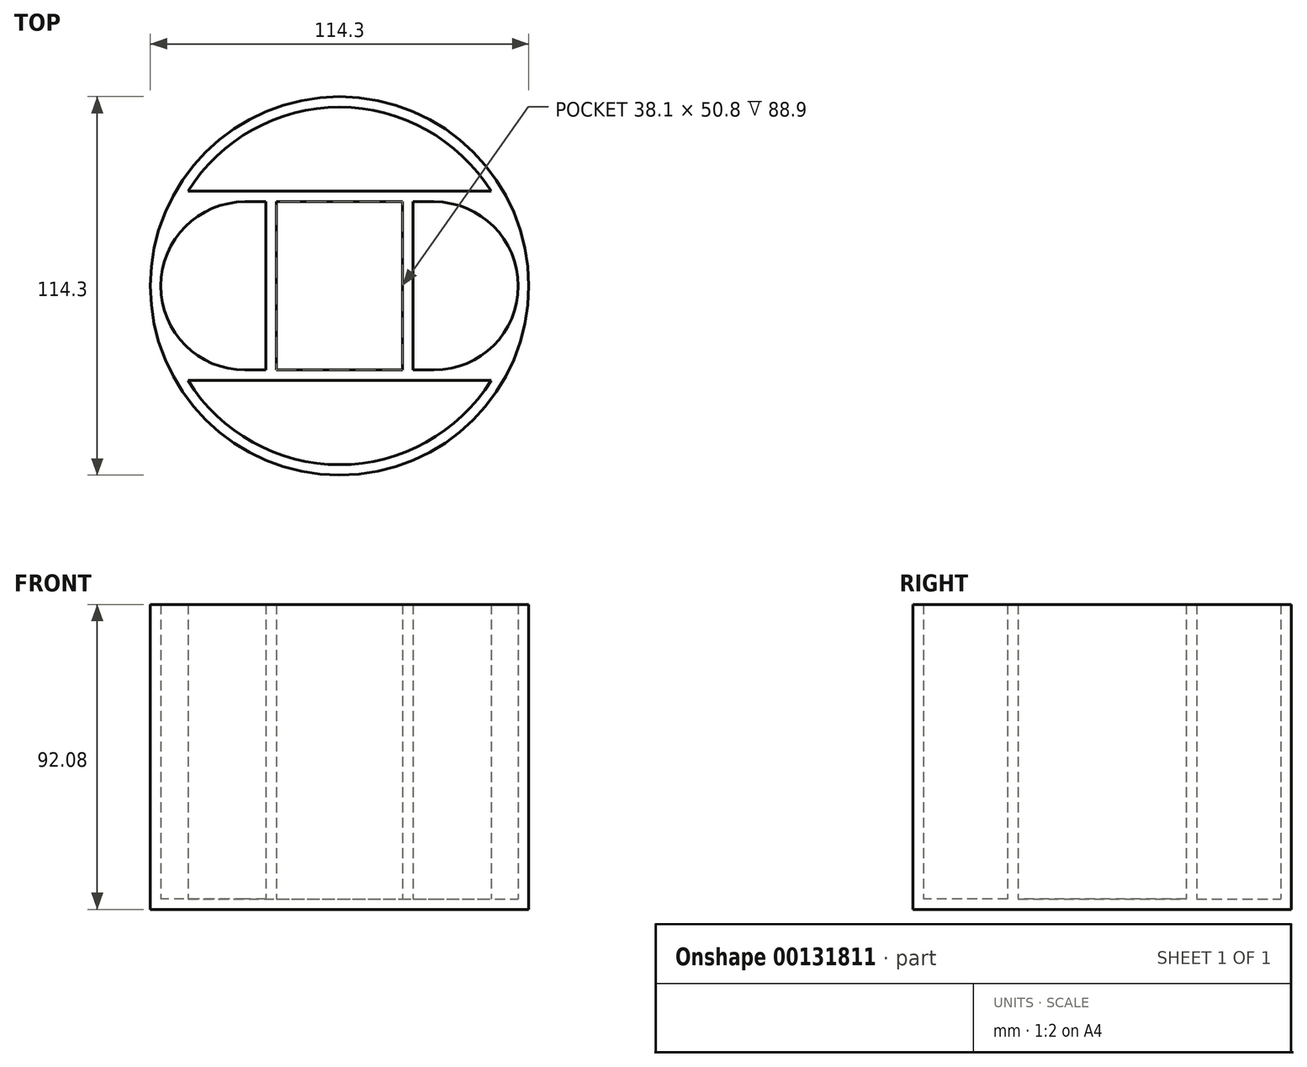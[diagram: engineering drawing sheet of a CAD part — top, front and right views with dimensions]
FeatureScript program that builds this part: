
annotation { "Feature Type Name" : "Feature", "Feature Type Description" : "" }
export const myFeature = defineFeature(function(context is Context, id is Id, definition is map)
    precondition{}
    {
        {
            var Q0;
            Q0=qCreatedBy(makeId("Top.planeOp"),FACE);
            var sketch = newSketch(context, id + "F2", { "sketchPlane" : qUnion([Q0])});
            skLineSegment(sketch, "E0.bottom", {"start": v(-22.23, 0) * mm, "end": v(-28.58, 0) * mm});
            skLineSegment(sketch, "E0.top", {"start": v(-22.22, 50.8) * mm, "end": v(-28.58, 50.8) * mm});
            skLineSegment(sketch, "E0.right", {"start": v(-28.58, 0) * mm, "end": v(-28.58, 50.8) * mm, "construction": true});
            skArc(sketch, "E1", {"start": v(-28.58, 50.8) * mm, "mid": v(-53.98, 25.4) * mm, "end": v(-28.58, 0) * mm});
            skLineSegment(sketch, "E2", {"start": v(-22.23, 0) * mm, "end": v(-22.23, 50.8) * mm});
            skLineSegment(sketch, "E3", {"start": v(0, 0) * mm, "end": v(0, 50.8) * mm, "construction": true});
            skLineSegment(sketch, "E4", {"start": v(0, 0) * mm, "end": v(-19.05, 0) * mm});
            skLineSegment(sketch, "E5", {"start": v(-19.05, 0) * mm, "end": v(-19.05, 50.8) * mm});
            skLineSegment(sketch, "E6", {"start": v(-19.05, 50.8) * mm, "end": v(0, 50.8) * mm});
            skCircle(sketch, "E7", {"center": v(0, 25.4) * mm, "radius": 57.15 * mm});
            skLineSegment(sketch, "E8.MirrorCS", {"start": v(19.05, 50.8) * mm, "end": v(0, 50.8) * mm});
            skLineSegment(sketch, "E9.MirrorCS", {"start": v(19.05, 0) * mm, "end": v(19.05, 50.8) * mm});
            skLineSegment(sketch, "E10.MirrorCS", {"start": v(0, 0) * mm, "end": v(19.05, 0) * mm});
            skLineSegment(sketch, "E11.MirrorCS", {"start": v(22.23, 0) * mm, "end": v(28.58, 0) * mm});
            skLineSegment(sketch, "E12.MirrorCS", {"start": v(22.23, 0) * mm, "end": v(22.23, 50.8) * mm});
            skLineSegment(sketch, "E13.MirrorCS", {"start": v(22.22, 50.8) * mm, "end": v(28.58, 50.8) * mm});
            skArc(sketch, "E14.MirrorCS", {"start": v(28.58, 50.8) * mm, "mid": v(53.98, 25.4) * mm, "end": v(28.58, 0) * mm});
            skArc(sketch, "E15.0", {"start": v(-45.8, -3.18) * mm, "mid": v(0, -28.58) * mm, "end": v(45.8, -3.17) * mm});
            skLineSegment(sketch, "E16", {"start": v(-45.8, 53.98) * mm, "end": v(45.8, 53.98) * mm});
            skLineSegment(sketch, "E17", {"start": v(0, 50.8) * mm, "end": v(0, 53.98) * mm, "construction": true});
            skLineSegment(sketch, "E18", {"start": v(-45.8, -3.18) * mm, "end": v(45.8, -3.18) * mm});
            skLineSegment(sketch, "E19", {"start": v(0, 0) * mm, "end": v(0, -3.18) * mm, "construction": true});
            skLineSegment(sketch, "E20", {"start": v(-19.05, 0) * mm, "end": v(-22.23, 0) * mm, "construction": true});
            skArc(sketch, "E21.trimOffspring", {"start": v(45.8, 53.98) * mm, "mid": v(0, 79.38) * mm, "end": v(-45.8, 53.98) * mm});
            skSolve(sketch);
        }
        {
            var Q0;
            Q0=makeQuery(id+"F2.imprint","IMPRINT",FACE,{"disambiguationData":[TD([[makeQuery(id+"F2.imprint","IMPRINT",EDGE,{"derivedFrom":sQuery(id+"F2.wireOp",EDGE,"E0.bottom")}),1.0]])]});
            var Q1;
            Q1=makeQuery(id+"F2.imprint","IMPRINT",FACE,{"disambiguationData":[TD([[makeQuery(id+"F2.imprint","IMPRINT",EDGE,{"derivedFrom":sQuery(id+"F2.wireOp",EDGE,"E0.left")}),-1.0]])]});
            extrude(context, id + "F3", {"entities" : qUnion([Q0, Q1]), "depth" : 88.9 * mm});
        }
        {
            var Q0;
            Q0=makeQuery(id+"F3.opExtrude","CAP_FACE",FACE,{"disambiguationData":[OSD([sQuery(id+"F2.wireOp",EDGE,"E0.bottom"),sQuery(id+"F2.wireOp",EDGE,"E0.top"),sQuery(id+"F2.wireOp",EDGE,"E1"),sQuery(id+"F2.wireOp",EDGE,"E2"),sQuery(id+"F2.wireOp",EDGE,"E4"),sQuery(id+"F2.wireOp",EDGE,"E5"),sQuery(id+"F2.wireOp",EDGE,"E6"),sQuery(id+"F2.wireOp",EDGE,"E7"),sQuery(id+"F2.wireOp",EDGE,"E8.MirrorCS"),sQuery(id+"F2.wireOp",EDGE,"E9.MirrorCS"),sQuery(id+"F2.wireOp",EDGE,"E10.MirrorCS"),sQuery(id+"F2.wireOp",EDGE,"E11.MirrorCS"),sQuery(id+"F2.wireOp",EDGE,"E12.MirrorCS"),sQuery(id+"F2.wireOp",EDGE,"E13.MirrorCS"),sQuery(id+"F2.wireOp",EDGE,"E14.MirrorCS"),sQuery(id+"F2.wireOp",EDGE,"E15.0"),sQuery(id+"F2.wireOp",EDGE,"E16"),sQuery(id+"F2.wireOp",EDGE,"E18"),sQuery(id+"F2.wireOp",EDGE,"E21.trimOffspring")])],"isStart":true});
            var sketch = newSketch(context, id + "F0", { "sketchPlane" : qUnion([Q0])});
            skCircle(sketch, "E22.0", {"center": v(0, -25.4) * mm, "radius": 57.15 * mm});
            skSolve(sketch);
        }
        {
            var Q0;
            Q0 = qSketchRegion(id + "F0", true);
            extrude(context, id + "F1", {"entities" : qUnion([Q0]), "operationType" : NewBodyOperationType.ADD, "depth" : 3.17 * mm});
        }
    });
